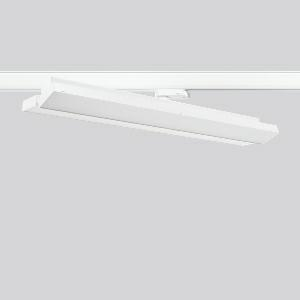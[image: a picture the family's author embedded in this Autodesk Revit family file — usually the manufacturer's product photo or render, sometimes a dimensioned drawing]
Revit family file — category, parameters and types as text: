
# Revit family: tx-move_742164_002_2_76_0ea8
name_source: partatom
category: Lighting Fixtures
units: mm (PartAtom-declared; Revit-internal decimal feet)

## family parameters
Cut with Voids When Loaded = No
Host = Face
Light Source = No
Part Type = Normal
Room Calculation Point = No
Round Connector Dimension = Use Diameter
Shared = No

## types (1)
- MultiLumen 1 (1 x LED Modul 927, 1775 lm, 2700)
    Apparent Load = 38 VA
    CIE Flux Codes = 47 79 96 100 100
    Color Rendering = 92
    Color Temperature = 2700
    Default Elevation = 1800 mm
    Description = Series: TX-MOVE
Multifunctional surface-mounted spotlight for area lighting. Very flat design. Housing: sheet steel, powder-coated. Rotation range: 356°. Swivel range: 90°. Consistent alignment possible with visible tilt scale. High-efficiency LED units with flush-mounted opal diffuser made of non-yellowing PMMA. Symmetrical wide beam light distribution. Best colour rendering with CRI >90 for fresh products and coloured textiles. With adapter for RZB 3-circuit DALI tracks. Suitable for Track on ceiling. MultiLumen: Luminous flux adjustable in 3 steps. Factory setting is the highest luminous flux. Environmentally friendly and resource-saving due to replaceable and recyclable components. 
Colour: traffic white, matt (RAL 9016)
Length: 570 mm
Width: 119 mm
Height: 88 mm
Lamp: LED
Socket: without socket
Colour temperature: 2700K
Colour rendering index (CRI): 90
System power: 38 W
Rated luminous flux: 3550 lm
Luminous efficiency: 93 lm/W
System power 2: 51 W
Rated luminous flux 2: 4650 lm
Luminous efficiency 2: 91 lm/W
System power 3: 62 W
Rated luminous flux 3: 5500 lm
Luminous efficiency 3: 89 lm/W
Control gear: Dimmable EVG, DALI
Protection class: I
Type of protection: IP 20
    Height = 75 mm
    Lamp = 1 x LED Modul 927
    Lamp Light Flux = 1775 lm
    Lamp count = 1
    Length = 569 mm
    Lifetime = 50000 h
    Luminous efficacy = 93 lm/W
    Manufacturer = RZB
    ModVariant = No
    Model = 742164.002.2.76
    Mounting Place = Ceiling
    Mounting Type = Surface mounted
    Number of Poles = 1
    OnlyDefault = Yes
    Power Factor = 1
    Product Name = TX-MOVE
    Product group = Track mounted projectors
    ProductGroupID = 301
    Protection Class = Protection class I
    Protection Degree = IP 20
    RLX_Detail_Level = 1
    RLX_Emergency_Light_Flux = 0 lm
    RLX_Emergency_Type = 0
    RLX_Emergency_Type_DB = No
    RlxData = <blob elided: 29945 chars, md5=36278591>
    Socket = socket
    Standby Power = 0 W
    System Light Flux = 3550 lm
    System Power = 38 W
    Type Comments = MultiLumen 1
    Type Image = 742164.002.jpg
    URL = http://relux.com
    VarID = multilumen_1
    Voltage = 0 V
    Weight = 0.00 kg
    Width = 119 mm

## geometry (parser evidence)
native form markers: Blend x4, Sweep x14
no freeform markers — native parametric forms only
